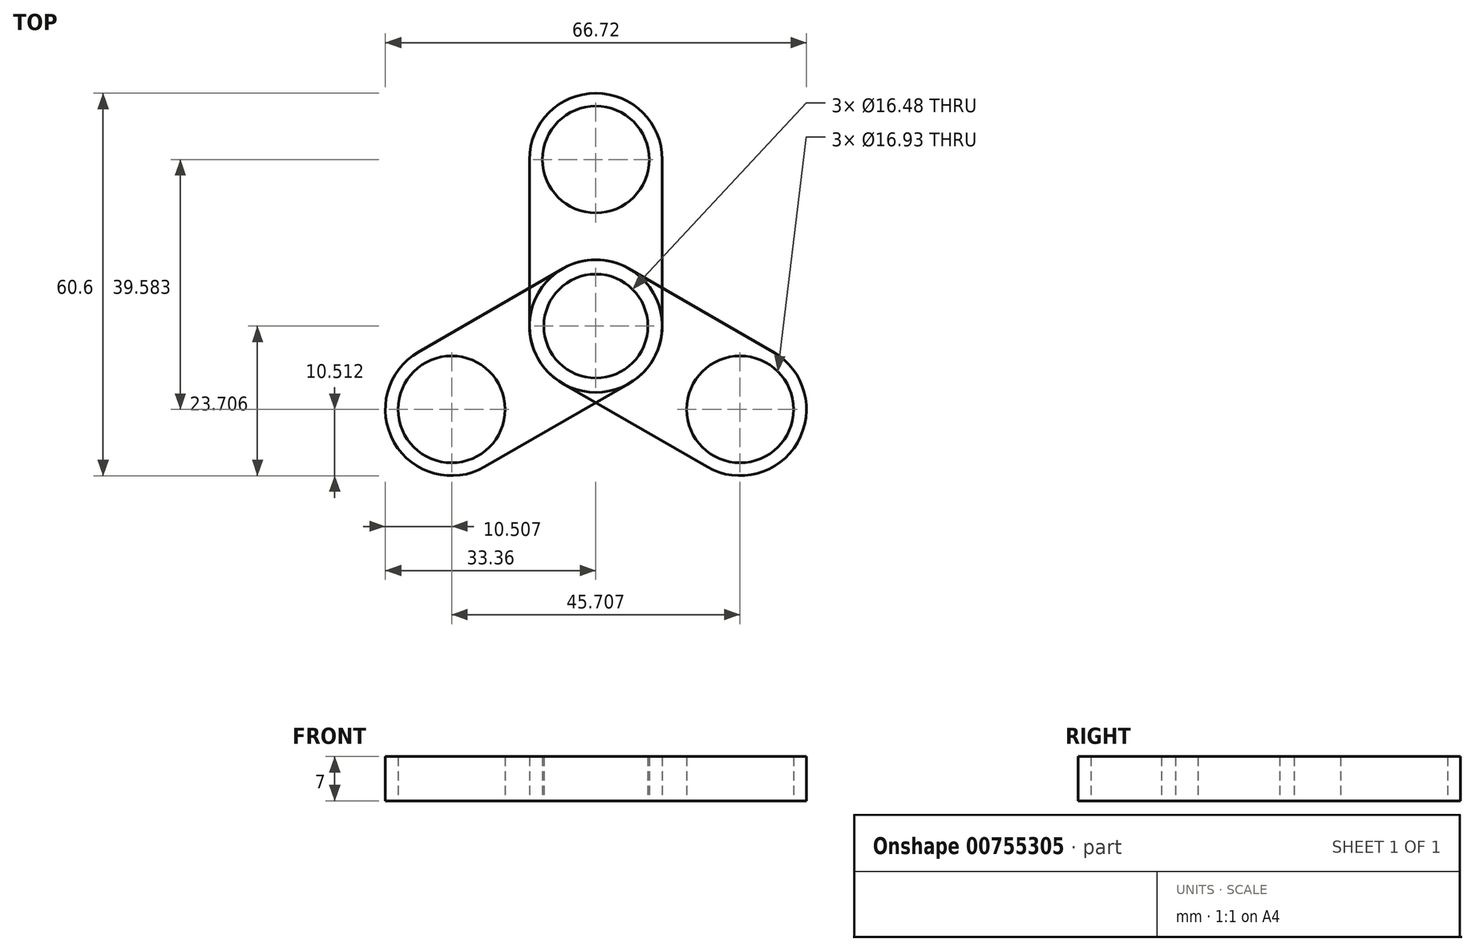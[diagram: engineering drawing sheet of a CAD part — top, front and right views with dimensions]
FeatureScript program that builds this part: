
annotation { "Feature Type Name" : "Feature", "Feature Type Description" : "" }
export const myFeature = defineFeature(function(context is Context, id is Id, definition is map)
    precondition{}
    {
        {
            var Q0;
            Q0=qCreatedBy(makeId("Top.planeOp"),FACE);
            var sketch = newSketch(context, id + "F0", { "sketchPlane" : qUnion([Q0])});
            skLineSegment(sketch, "E0.bottom", {"start": v(6.82, 12) * mm, "end": v(27.84, 12) * mm});
            skLineSegment(sketch, "E0.top", {"start": v(6.82, -14.38) * mm, "end": v(27.84, -14.38) * mm});
            skLineSegment(sketch, "E0.left", {"start": v(6.82, 12) * mm, "end": v(6.82, -14.38) * mm});
            skLineSegment(sketch, "E0.right", {"start": v(27.84, 12) * mm, "end": v(27.84, -14.38) * mm});
            skCircle(sketch, "E1", {"center": v(17.33, 12) * mm, "radius": 10.5 * mm});
            skCircle(sketch, "E2", {"center": v(17.33, -14.38) * mm, "radius": 10.5 * mm});
            skCircle(sketch, "E3", {"center": v(17.33, -14.38) * mm, "radius": 8.24 * mm});
            skCircle(sketch, "E4", {"center": v(17.33, 12) * mm, "radius": 8.47 * mm});
            skSolve(sketch);
        }
        {
            var Q0;
            {var subQ0=sQuery(id+"F0.wireOp",EDGE,"E0.left");Q0=makeQuery(id+"F0.imprint","IMPRINT",FACE,{"disambiguationData":[TD([[makeQuery(id+"F0.imprint","IMPRINT",EDGE,{"derivedFrom":subQ0}),1.0]])]});}
            var Q1;
            {var subQ1=sQuery(id+"F0.wireOp",EDGE,"E0.bottom");var subQ3=sQuery(id+"F0.wireOp",EDGE,"E4");var subQ4=makeQuery(id+"F0.imprint","INTERSECT",VERTEX,{"disambiguationData":[OD(0.0)],"derivedFrom":[subQ1,subQ3]});Q1=makeQuery(id+"F0.imprint","IMPRINT",FACE,{"disambiguationData":[TD([[makeQuery(id+"F0.imprint","IMPRINT",EDGE,{"disambiguationData":[TD([[subQ4,1.0]])],"derivedFrom":subQ3}),-1.0]])]});}
            var Q2;
            {var subQ1=sQuery(id+"F0.wireOp",EDGE,"E0.bottom");var subQ3=sQuery(id+"F0.wireOp",EDGE,"E4");var subQ4=makeQuery(id+"F0.imprint","INTERSECT",VERTEX,{"disambiguationData":[OD(0.0)],"derivedFrom":[subQ1,subQ3]});Q2=makeQuery(id+"F0.imprint","IMPRINT",FACE,{"disambiguationData":[TD([[makeQuery(id+"F0.imprint","IMPRINT",EDGE,{"disambiguationData":[TD([[subQ4,-1.0]])],"derivedFrom":subQ3}),-1.0]])]});}
            var Q3;
            {var subQ1=sQuery(id+"F0.wireOp",EDGE,"E0.top");var subQ3=sQuery(id+"F0.wireOp",EDGE,"E3");var subQ4=makeQuery(id+"F0.imprint","INTERSECT",VERTEX,{"disambiguationData":[OD(0.0)],"derivedFrom":[subQ1,subQ3]});Q3=makeQuery(id+"F0.imprint","IMPRINT",FACE,{"disambiguationData":[TD([[makeQuery(id+"F0.imprint","IMPRINT",EDGE,{"disambiguationData":[TD([[subQ4,1.0]])],"derivedFrom":subQ3}),-1.0]])]});}
            var Q4;
            {var subQ1=sQuery(id+"F0.wireOp",EDGE,"E0.top");var subQ3=sQuery(id+"F0.wireOp",EDGE,"E3");var subQ4=makeQuery(id+"F0.imprint","INTERSECT",VERTEX,{"disambiguationData":[OD(0.0)],"derivedFrom":[subQ1,subQ3]});Q4=makeQuery(id+"F0.imprint","IMPRINT",FACE,{"disambiguationData":[TD([[makeQuery(id+"F0.imprint","IMPRINT",EDGE,{"disambiguationData":[TD([[subQ4,-1.0]])],"derivedFrom":subQ3}),-1.0]])]});}
            extrude(context, id + "F1", {"entities" : qUnion([Q0, Q1, Q2, Q3, Q4]), "depth" : 7 * mm, "offsetDistance" : 25 * mm});
        }
        {
            var Q0;
            Q0=makeQuery(id+"F1.opExtrude","SWEPT_BODY",BODY,{"disambiguationData":[OSD([sQuery(id+"F0.wireOp",EDGE,"E0.left"),sQuery(id+"F0.wireOp",EDGE,"E0.right"),sQuery(id+"F0.wireOp",EDGE,"E1"),sQuery(id+"F0.wireOp",EDGE,"E2"),sQuery(id+"F0.wireOp",EDGE,"E3"),sQuery(id+"F0.wireOp",EDGE,"E4")])]});
            var Q1;
            Q1=makeQuery(id+"F1.opExtrude","SWEPT_FACE",FACE,{"disambiguationData":[OSD([sQuery(id+"F0.wireOp",EDGE,"E2")])]});
            circularPattern(context, id + "F2", {"entities" : qUnion([Q0]), "axis" : qUnion([Q1]), "angle" : 360 * degree, "instanceCount" : 3, "equalSpace" : true});
        }
    });
